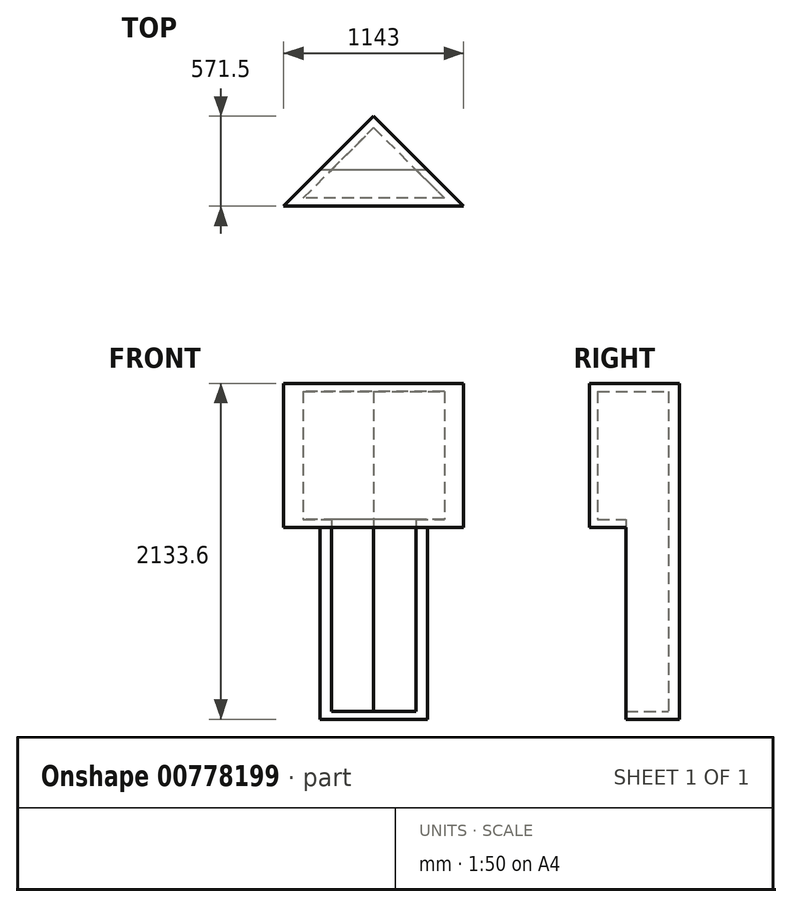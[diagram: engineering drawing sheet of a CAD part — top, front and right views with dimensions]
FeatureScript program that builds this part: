
annotation { "Feature Type Name" : "Feature", "Feature Type Description" : "" }
export const myFeature = defineFeature(function(context is Context, id is Id, definition is map)
    precondition{}
    {
        {
            var Q0;
            Q0=qCreatedBy(makeId("Top.planeOp"),FACE);
            var sketch = newSketch(context, id + "F0", { "sketchPlane" : qUnion([Q0])});
            skLineSegment(sketch, "E0", {"start": v(-341.25, -341.25) * mm, "end": v(0, 0) * mm});
            skLineSegment(sketch, "E1", {"start": v(0, 0) * mm, "end": v(341.25, -341.25) * mm});
            skLineSegment(sketch, "E2", {"start": v(341.25, -341.25) * mm, "end": v(-341.25, -341.25) * mm});
            skLineSegment(sketch, "E3", {"start": v(0, -512.16) * mm, "end": v(0, 218.92) * mm, "construction": true});
            skLineSegment(sketch, "E4", {"start": v(-558.8, -559.42) * mm, "end": v(558.8, -559.42) * mm});
            skPoint(sketch, "E5", {"position": v(0, -341.25) * mm});
            skLineSegment(sketch, "E6", {"start": v(0, 0) * mm, "end": v(869.47, -869.47) * mm, "construction": true});
            skLineSegment(sketch, "E7", {"start": v(0, 0) * mm, "end": v(-803.18, -803.18) * mm, "construction": true});
            skSolve(sketch);
        }
        {
            var Q0;
            Q0=makeQuery(id+"F0.imprint","IMPRINT",FACE,{"disambiguationData":[TD([[makeQuery(id+"F0.imprint","IMPRINT",EDGE,{"derivedFrom":sQuery(id+"F0.wireOp",EDGE,"E0")}),-1.0]])]});
            extrude(context, id + "F1", {"entities" : qUnion([Q0]), "depth" : 1219.2 * mm, "offsetDistance" : 25.4 * mm});
        }
        {
            var Q0;
            Q0=makeQuery(id+"F1.opExtrude","CAP_FACE",FACE,{"disambiguationData":[OSD([sQuery(id+"F0.wireOp",EDGE,"E0"),sQuery(id+"F0.wireOp",EDGE,"E1"),sQuery(id+"F0.wireOp",EDGE,"E2")])],"isStart":false});
            var sketch = newSketch(context, id + "F2", { "sketchPlane" : qUnion([Q0])});
            skLineSegment(sketch, "E8", {"start": v(0, 0) * mm, "end": v(-571.5, -571.5) * mm});
            skLineSegment(sketch, "E9", {"start": v(0, 0) * mm, "end": v(571.5, -571.5) * mm});
            skLineSegment(sketch, "E10", {"start": v(571.5, -571.5) * mm, "end": v(-571.5, -571.5) * mm});
            skSolve(sketch);
        }
        {
            var Q0;
            {var subQ1=makeQuery(id+"F1.opExtrude","CAP_EDGE",EDGE,{"disambiguationData":[OSD([sQuery(id+"F0.wireOp",EDGE,"E2")])],"isStart":false});Q0=makeQuery(id+"F2.imprint","IMPRINT",FACE,{"disambiguationData":[TD([[makeQuery(id+"F2.imprint","IMPRINT",EDGE,{"derivedFrom":subQ1}),-1.0]])]});}
            var Q1;
            {var subQ2=sQuery(id+"F2.wireOp",EDGE,"E10");Q1=makeQuery(id+"F2.imprint","IMPRINT",FACE,{"disambiguationData":[TD([[makeQuery(id+"F2.imprint","IMPRINT",EDGE,{"derivedFrom":subQ2}),-1.0]])]});}
            extrude(context, id + "F3", {"entities" : qUnion([Q0, Q1]), "operationType" : NewBodyOperationType.ADD, "depth" : 914.4 * mm, "offsetDistance" : 25.4 * mm});
        }
        {
            var Q0;
            Q0=makeQuery(id+"F1.opExtrude","SWEPT_FACE",FACE,{"disambiguationData":[OSD([sQuery(id+"F0.wireOp",EDGE,"E2")])]});
            shell(context, id + "F4", {"entities" : qUnion([Q0]), "thickness" : 50.8 * mm});
        }
    });
